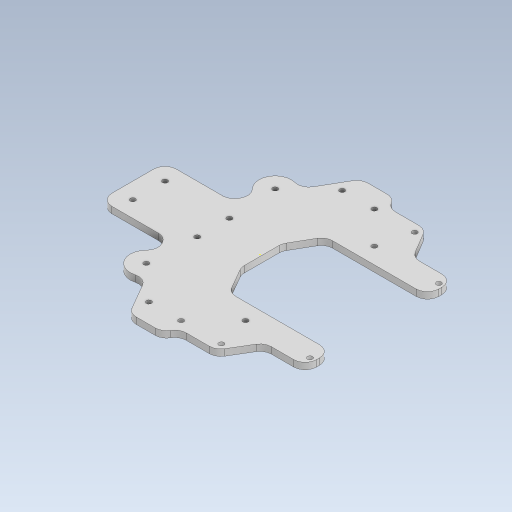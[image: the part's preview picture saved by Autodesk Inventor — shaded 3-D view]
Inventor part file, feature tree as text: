
AUTODESK INVENTOR PART (.ipt)
format: ipt  version: 2023.5 (Build 275446000, 446)  size: 464,896 bytes
history: native  units: mm
features: sketch x2, extrude x2, fillet x1
ambient origin geometry x8: Origin, YZ Plane, XZ Plane, XY Plane, X Axis, Y Axis, Z Axis, Center Point
bodies: Solid1 (feature_tree)
feature tree (5):
  sketch  "Sketch1"  dims[d0=3.2mm d3=3.2mm]
  extrude  "Extrusion1"  Depth=3.2mm
  sketch  "Sketch2"  dims[d5=3.2mm d6=50.0mm d15=20.0mm d16=40.0mm d17=120.0deg d18=20.0mm d23=4.0mm d24=0.0mm d25=3.2mm d27=40.0mm d28=120.0deg d29=3.2mm d30=40.0mm d31=55.0mm d32=15.981mm d33=120.0deg d34=4.0mm d35=0.0mm d36=3.2mm d37=30.0mm d38=20.0mm d39=3.2mm d40=25.0mm d41=7.0mm]
  extrude  "Extrusion2"  Depth=50.0mm
  fillet  "Fillet1"  Radius=20.0mm
